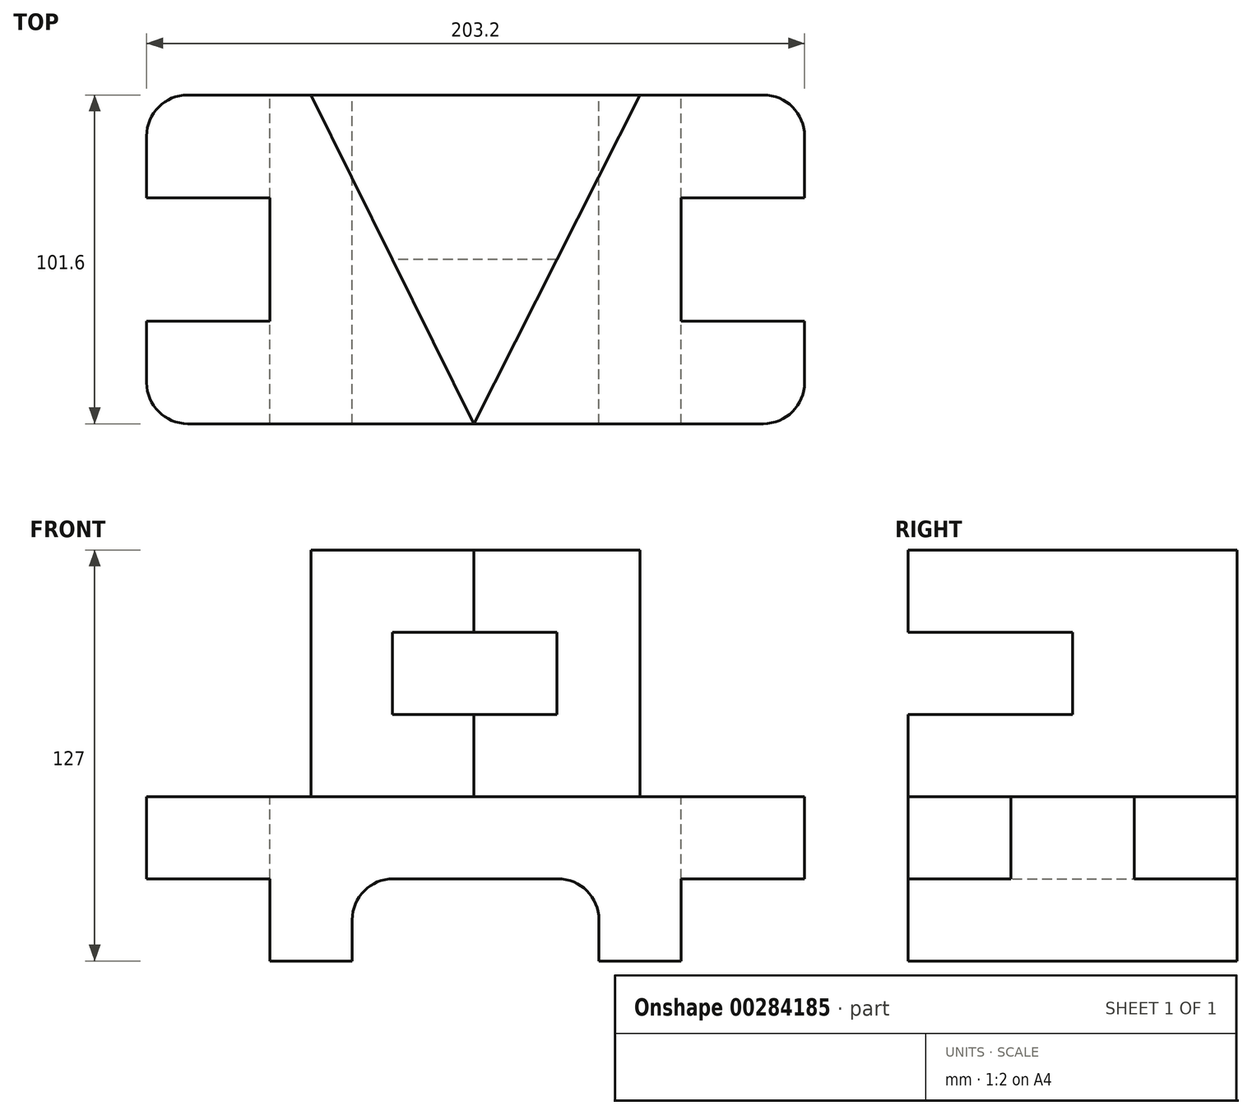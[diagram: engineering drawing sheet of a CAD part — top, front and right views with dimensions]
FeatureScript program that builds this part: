
annotation { "Feature Type Name" : "Feature", "Feature Type Description" : "" }
export const myFeature = defineFeature(function(context is Context, id is Id, definition is map)
    precondition{}
    {
        {
            var Q0;
            Q0=qCreatedBy(makeId("Front.planeOp"),FACE);
            var sketch = newSketch(context, id + "F0", { "sketchPlane" : qUnion([Q0])});
            skLineSegment(sketch, "E0", {"start": v(-101.08, 0) * mm, "end": v(-62.98, 0) * mm});
            skLineSegment(sketch, "E1", {"start": v(-62.98, 0) * mm, "end": v(-62.98, -25.4) * mm});
            skLineSegment(sketch, "E2", {"start": v(-62.98, -25.4) * mm, "end": v(-37.58, -25.4) * mm});
            skLineSegment(sketch, "E3", {"start": v(-37.58, -25.4) * mm, "end": v(-37.58, 0) * mm});
            skLineSegment(sketch, "E4", {"start": v(-37.58, 0) * mm, "end": v(38.62, 0) * mm});
            skLineSegment(sketch, "E5", {"start": v(38.62, 0) * mm, "end": v(38.62, -25.4) * mm});
            skLineSegment(sketch, "E6", {"start": v(38.62, -25.4) * mm, "end": v(64.02, -25.4) * mm});
            skLineSegment(sketch, "E7", {"start": v(64.02, -25.4) * mm, "end": v(64.02, 0) * mm});
            skLineSegment(sketch, "E8", {"start": v(64.02, 0) * mm, "end": v(102.12, 0) * mm});
            skLineSegment(sketch, "E9", {"start": v(102.12, 0) * mm, "end": v(102.12, 25.4) * mm});
            skLineSegment(sketch, "E10", {"start": v(102.12, 25.4) * mm, "end": v(51.32, 25.4) * mm});
            skLineSegment(sketch, "E11", {"start": v(51.32, 25.4) * mm, "end": v(51.32, 101.6) * mm});
            skLineSegment(sketch, "E12", {"start": v(51.32, 101.6) * mm, "end": v(-50.28, 101.6) * mm});
            skLineSegment(sketch, "E13", {"start": v(-50.28, 101.6) * mm, "end": v(-50.28, 25.4) * mm});
            skLineSegment(sketch, "E14", {"start": v(-50.28, 25.4) * mm, "end": v(-101.08, 25.4) * mm});
            skLineSegment(sketch, "E15", {"start": v(-101.08, 25.4) * mm, "end": v(-101.08, 0) * mm});
            skSolve(sketch);
        }
        {
            var Q0;
            Q0=makeQuery(id+"F0.imprint","IMPRINT",FACE,{"disambiguationData":[TD([[makeQuery(id+"F0.imprint","IMPRINT",EDGE,{"derivedFrom":sQuery(id+"F0.wireOp",EDGE,"E0")}),1.0]])]});
            extrude(context, id + "F1", {"entities" : qUnion([Q0]), "depth" : 101.6 * mm, "symmetric" : true});
        }
        {
            var Q0;
            Q0=makeQuery(id+"F1.opExtrude","CAP_FACE",FACE,{"disambiguationData":[OSD([sQuery(id+"F0.wireOp",EDGE,"E0"),sQuery(id+"F0.wireOp",EDGE,"E1"),sQuery(id+"F0.wireOp",EDGE,"E2"),sQuery(id+"F0.wireOp",EDGE,"E3"),sQuery(id+"F0.wireOp",EDGE,"E4"),sQuery(id+"F0.wireOp",EDGE,"E5"),sQuery(id+"F0.wireOp",EDGE,"E6"),sQuery(id+"F0.wireOp",EDGE,"E7"),sQuery(id+"F0.wireOp",EDGE,"E8"),sQuery(id+"F0.wireOp",EDGE,"E9"),sQuery(id+"F0.wireOp",EDGE,"E10"),sQuery(id+"F0.wireOp",EDGE,"E11"),sQuery(id+"F0.wireOp",EDGE,"E12"),sQuery(id+"F0.wireOp",EDGE,"E13"),sQuery(id+"F0.wireOp",EDGE,"E14"),sQuery(id+"F0.wireOp",EDGE,"E15")])],"isStart":false});
            var sketch = newSketch(context, id + "F2", { "sketchPlane" : qUnion([Q0])});
            skLineSegment(sketch, "E16", {"start": v(71.14, 101.6) * mm, "end": v(71.14, 76.2) * mm});
            skLineSegment(sketch, "E17", {"start": v(113.4, 25.4) * mm, "end": v(113.4, 50.8) * mm});
            skLineSegment(sketch, "E18", {"start": v(51.32, 76.2) * mm, "end": v(51.32, 50.8) * mm});
            skLineSegment(sketch, "E19", {"start": v(51.32, 50.8) * mm, "end": v(-50.28, 50.8) * mm});
            skLineSegment(sketch, "E20", {"start": v(-50.28, 50.8) * mm, "end": v(-50.28, 76.2) * mm});
            skLineSegment(sketch, "E21", {"start": v(-50.28, 76.2) * mm, "end": v(51.32, 76.2) * mm});
            skSolve(sketch);
        }
        {
            var Q0;
            Q0=makeQuery(id+"F2.imprint","IMPRINT",FACE,{"disambiguationData":[TD([[makeQuery(id+"F2.imprint","IMPRINT",EDGE,{"derivedFrom":sQuery(id+"F2.wireOp",EDGE,"E18")}),1.0]])]});
            extrude(context, id + "F3", {"entities" : qUnion([Q0]), "operationType" : NewBodyOperationType.REMOVE, "oppositeDirection" : true, "depth" : 50.8 * mm});
        }
        {
            var Q0;
            Q0=makeQuery(id+"F1.opExtrude","SWEPT_FACE",FACE,{"disambiguationData":[OSD([sQuery(id+"F0.wireOp",EDGE,"E12")])]});
            var sketch = newSketch(context, id + "F4", { "sketchPlane" : qUnion([Q0])});
            skLineSegment(sketch, "E22", {"start": v(-50.28, 50.8) * mm, "end": v(0, -50.8) * mm});
            skLineSegment(sketch, "E23", {"start": v(0, -50.8) * mm, "end": v(51.32, 50.8) * mm});
            skLineSegment(sketch, "E24", {"start": v(51.32, 50.8) * mm, "end": v(-50.28, 50.8) * mm});
            skSolve(sketch);
        }
        {
            var Q0;
            {var subQ0=sQuery(id+"F4.wireOp",EDGE,"E23");Q0=makeQuery(id+"F4.imprint","IMPRINT",FACE,{"disambiguationData":[TD([[makeQuery(id+"F4.imprint","IMPRINT",EDGE,{"derivedFrom":subQ0}),-1.0]])]});}
            var Q1;
            {var subQ0=sQuery(id+"F4.wireOp",EDGE,"E22");Q1=makeQuery(id+"F4.imprint","IMPRINT",FACE,{"disambiguationData":[TD([[makeQuery(id+"F4.imprint","IMPRINT",EDGE,{"derivedFrom":subQ0}),-1.0]])]});}
            extrude(context, id + "F5", {"entities" : qUnion([Q0, Q1]), "operationType" : NewBodyOperationType.REMOVE, "oppositeDirection" : true, "depth" : 76.2 * mm});
        }
        {
            var Q0;
            Q0=makeQuery(id+"F5.boolean.opBoolean","MERGE",FACE,{"derivedFrom":[makeQuery(id+"F1.opExtrude","SWEPT_FACE",FACE,{"disambiguationData":[OSD([sQuery(id+"F0.wireOp",EDGE,"E10")])]}),makeQuery(id+"F5.opExtrude","CAP_FACE",FACE,{"disambiguationData":[OSD([sQuery(id+"F0.wireOp",EDGE,"E11"),sQuery(id+"F0.wireOp",EDGE,"E12"),sQuery(id+"F4.wireOp",EDGE,"E23")])],"isStart":false})]});
            var sketch = newSketch(context, id + "F6", { "sketchPlane" : qUnion([Q0])});
            skLineSegment(sketch, "E25", {"start": v(123.47, -50.8) * mm, "end": v(123.47, -19.05) * mm});
            skLineSegment(sketch, "E26", {"start": v(119.05, 50.8) * mm, "end": v(119.05, 19.05) * mm});
            skLineSegment(sketch, "E27", {"start": v(102.12, 65.07) * mm, "end": v(64.02, 65.07) * mm});
            skLineSegment(sketch, "E28", {"start": v(102.12, -74.22) * mm, "end": v(64.02, -74.22) * mm});
            skLineSegment(sketch, "E29", {"start": v(102.12, 19.05) * mm, "end": v(64.02, 19.05) * mm});
            skLineSegment(sketch, "E30", {"start": v(64.02, 19.05) * mm, "end": v(64.02, -19.05) * mm});
            skLineSegment(sketch, "E31", {"start": v(64.02, -19.05) * mm, "end": v(102.12, -19.05) * mm});
            skLineSegment(sketch, "E32", {"start": v(102.12, -19.05) * mm, "end": v(102.12, 19.05) * mm});
            skSolve(sketch);
        }
        {
            var Q0;
            Q0=makeQuery(id+"F6.imprint","IMPRINT",FACE,{"disambiguationData":[TD([[makeQuery(id+"F6.imprint","IMPRINT",EDGE,{"derivedFrom":sQuery(id+"F6.wireOp",EDGE,"E29")}),1.0]])]});
            extrude(context, id + "F7", {"entities" : qUnion([Q0]), "operationType" : NewBodyOperationType.REMOVE, "oppositeDirection" : true, "depth" : 25.4 * mm});
        }
        {
            var Q0;
            Q0=makeQuery(id+"F5.boolean.opBoolean","MERGE",FACE,{"derivedFrom":[makeQuery(id+"F1.opExtrude","SWEPT_FACE",FACE,{"disambiguationData":[OSD([sQuery(id+"F0.wireOp",EDGE,"E14")])]}),makeQuery(id+"F5.opExtrude","CAP_FACE",FACE,{"disambiguationData":[OSD([sQuery(id+"F0.wireOp",EDGE,"E12"),sQuery(id+"F0.wireOp",EDGE,"E13"),sQuery(id+"F4.wireOp",EDGE,"E22")])],"isStart":false})]});
            var sketch = newSketch(context, id + "F8", { "sketchPlane" : qUnion([Q0])});
            skLineSegment(sketch, "E33", {"start": v(-101.08, 68.92) * mm, "end": v(-62.98, 68.92) * mm});
            skLineSegment(sketch, "E34", {"start": v(-125.08, 50.8) * mm, "end": v(-125.08, 19.05) * mm});
            skLineSegment(sketch, "E35", {"start": v(-62.98, -62.06) * mm, "end": v(-101.08, -62.06) * mm});
            skLineSegment(sketch, "E36", {"start": v(-120.9, -50.8) * mm, "end": v(-120.9, -19.05) * mm});
            skLineSegment(sketch, "E37", {"start": v(-101.08, 19.05) * mm, "end": v(-62.98, 19.05) * mm});
            skLineSegment(sketch, "E38", {"start": v(-62.98, 19.05) * mm, "end": v(-62.98, -19.05) * mm});
            skLineSegment(sketch, "E39", {"start": v(-62.98, -19.05) * mm, "end": v(-101.08, -19.05) * mm});
            skLineSegment(sketch, "E40", {"start": v(-101.08, -19.05) * mm, "end": v(-101.08, 19.05) * mm});
            skSolve(sketch);
        }
        {
            var Q0;
            Q0=makeQuery(id+"F8.imprint","IMPRINT",FACE,{"disambiguationData":[TD([[makeQuery(id+"F8.imprint","IMPRINT",EDGE,{"derivedFrom":sQuery(id+"F8.wireOp",EDGE,"E37")}),-1.0]])]});
            extrude(context, id + "F9", {"entities" : qUnion([Q0]), "operationType" : NewBodyOperationType.REMOVE, "oppositeDirection" : true, "depth" : 25.4 * mm});
        }
        {
            var Q0;
            Q0=makeQuery(id+"F1.opExtrude","SWEPT_EDGE",EDGE,{"disambiguationData":[OSD([sQuery(id+"F0.wireOp",EDGE,"E3"),sQuery(id+"F0.wireOp",EDGE,"E4")])]});
            var Q1;
            Q1=makeQuery(id+"F1.opExtrude","SWEPT_EDGE",EDGE,{"disambiguationData":[OSD([sQuery(id+"F0.wireOp",EDGE,"E4"),sQuery(id+"F0.wireOp",EDGE,"E5")])]});
            fillet(context, id + "F10", {"entities" : qUnion([Q0, Q1]), "radius" : 12.7 * mm, "tangentPropagation" : true, "allowEdgeOverflow" : false});
        }
        {
            var Q0;
            Q0=makeQuery(id+"F1.opExtrude","CAP_EDGE",EDGE,{"disambiguationData":[OSD([sQuery(id+"F0.wireOp",EDGE,"E9")])],"isStart":false});
            var Q1;
            Q1=makeQuery(id+"F1.opExtrude","CAP_EDGE",EDGE,{"disambiguationData":[OSD([sQuery(id+"F0.wireOp",EDGE,"E9")])],"isStart":true});
            var Q2;
            Q2=makeQuery(id+"F1.opExtrude","CAP_EDGE",EDGE,{"disambiguationData":[OSD([sQuery(id+"F0.wireOp",EDGE,"E15")])],"isStart":false});
            var Q3;
            Q3=makeQuery(id+"F1.opExtrude","CAP_EDGE",EDGE,{"disambiguationData":[OSD([sQuery(id+"F0.wireOp",EDGE,"E15")])],"isStart":true});
            fillet(context, id + "F11", {"entities" : qUnion([Q0, Q1, Q2, Q3]), "radius" : 12.7 * mm, "tangentPropagation" : true, "allowEdgeOverflow" : false});
        }
    });
